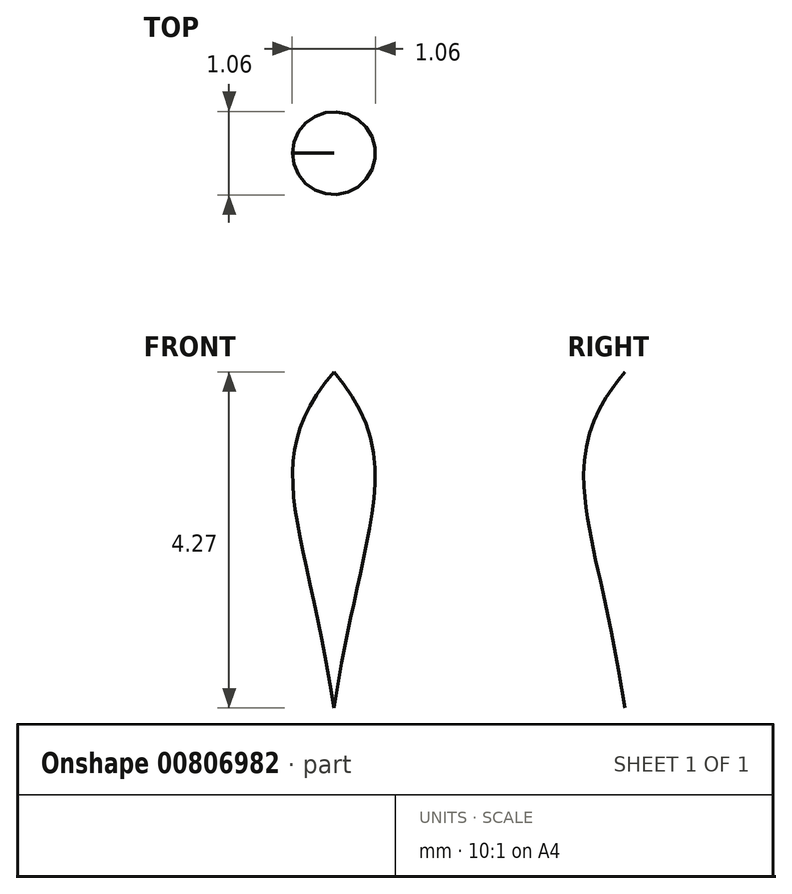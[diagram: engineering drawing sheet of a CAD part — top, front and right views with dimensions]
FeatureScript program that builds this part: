
annotation { "Feature Type Name" : "Feature", "Feature Type Description" : "" }
export const myFeature = defineFeature(function(context is Context, id is Id, definition is map)
    precondition{}
    {
        {
            var Q0;
            Q0=qCreatedBy(makeId("Front.planeOp"),FACE);
            var sketch = newSketch(context, id + "F0", { "sketchPlane" : qUnion([Q0])});
            skFitSpline(sketch, "E0", {"points": [v(0, 0) * mm, v(7.01, -24.78) * mm, v(34.64, 0) * mm, v(25.48, 30.33) * mm, v(32.98, 43.03) * mm, v(24.47, 34.52) * mm, v(28.02, 6.88) * mm, v(21.15, -2.42) * mm, v(11.92, 7.68) * mm, v(0, 4.27) * mm, v(0, 0) * mm]});
            skLineSegment(sketch, "E1", {"start": v(0, 42.44) * mm, "end": v(0, -15.46) * mm});
            skFitSpline(sketch, "E2", {"points": [v(25.94, 32.29) * mm, v(38.42, 35.38) * mm, v(51.7, 21.67) * mm, v(46.93, 2.2) * mm, v(21.79, -19.58) * mm], "startDerivative": vector(61.66, 31.65) * mm, "endDerivative": vector(-91.52, -65.36) * mm});
            skSolve(sketch);
        }
        {
            var Q0;
            {var subQ0=sQuery(id+"F0.wireOp",EDGE,"E1");var subQ1=sQuery(id+"F0.wireOp",EDGE,"E0");var subQ2=makeQuery(id+"F0.imprint","INTERSECT",VERTEX,{"disambiguationData":[OD(0.0)],"derivedFrom":[subQ1,subQ0]});Q0=makeQuery(id+"F0.imprint","IMPRINT",FACE,{"disambiguationData":[TD([[makeQuery(id+"F0.imprint","IMPRINT",EDGE,{"disambiguationData":[TD([[subQ2,-1.0]])],"derivedFrom":subQ1}),1.0]])]});}
            var Q1;
            Q1=sQuery(id+"F0.wireOp",EDGE,"E1");
            revolve(context, id + "F1", {"surfaceOperationType" : NewSurfaceOperationType.NEW, "entities" : qUnion([Q0]), "axis" : qUnion([Q1]), "revolveType" : RevolveType.FULL});
        }
        {
            var Q0;
            Q0=qCreatedBy(makeId("Right.planeOp"),FACE);
            var sketch = newSketch(context, id + "F2", { "sketchPlane" : qUnion([Q0])});
            skFitSpline(sketch, "E3", {"points": [v(-27.05, 22.37) * mm, v(-49.01, 34) * mm, v(-63.99, 27.55) * mm, v(-65.92, 26.33) * mm, v(-71.31, 11.1) * mm, v(-71.02, 10.67) * mm, v(-28.34, -11.73) * mm], "startDerivative": vector(-81.86, 60.17) * mm, "endDerivative": vector(187.15, -99.32) * mm});
            skSolve(sketch);
        }
        {
            var Q0;
            Q0=qCreatedBy(makeId("Front.planeOp"),FACE);
            var sketch = newSketch(context, id + "F3", { "sketchPlane" : qUnion([Q0])});
            skCircle(sketch, "E4", {"center": v(7.93, 25.45) * mm, "radius": 4.32 * mm});
            skSolve(sketch);
        }
        {
            var Q0;
            Q0=sQuery(id+"F2.wireOp",EDGE,"E3");
            var Q1;
            Q1=sQuery(id+"F2.wireOp",VERTEX,"E3.end");
            cPlane(context, id + "F4", {"entities" : qUnion([Q0, Q1]), "cplaneType" : CPlaneType.CURVE_POINT, "offset" : 25.4 * mm, "width" : 152.4 * mm, "height" : 152.4 * mm});
        }
    });
